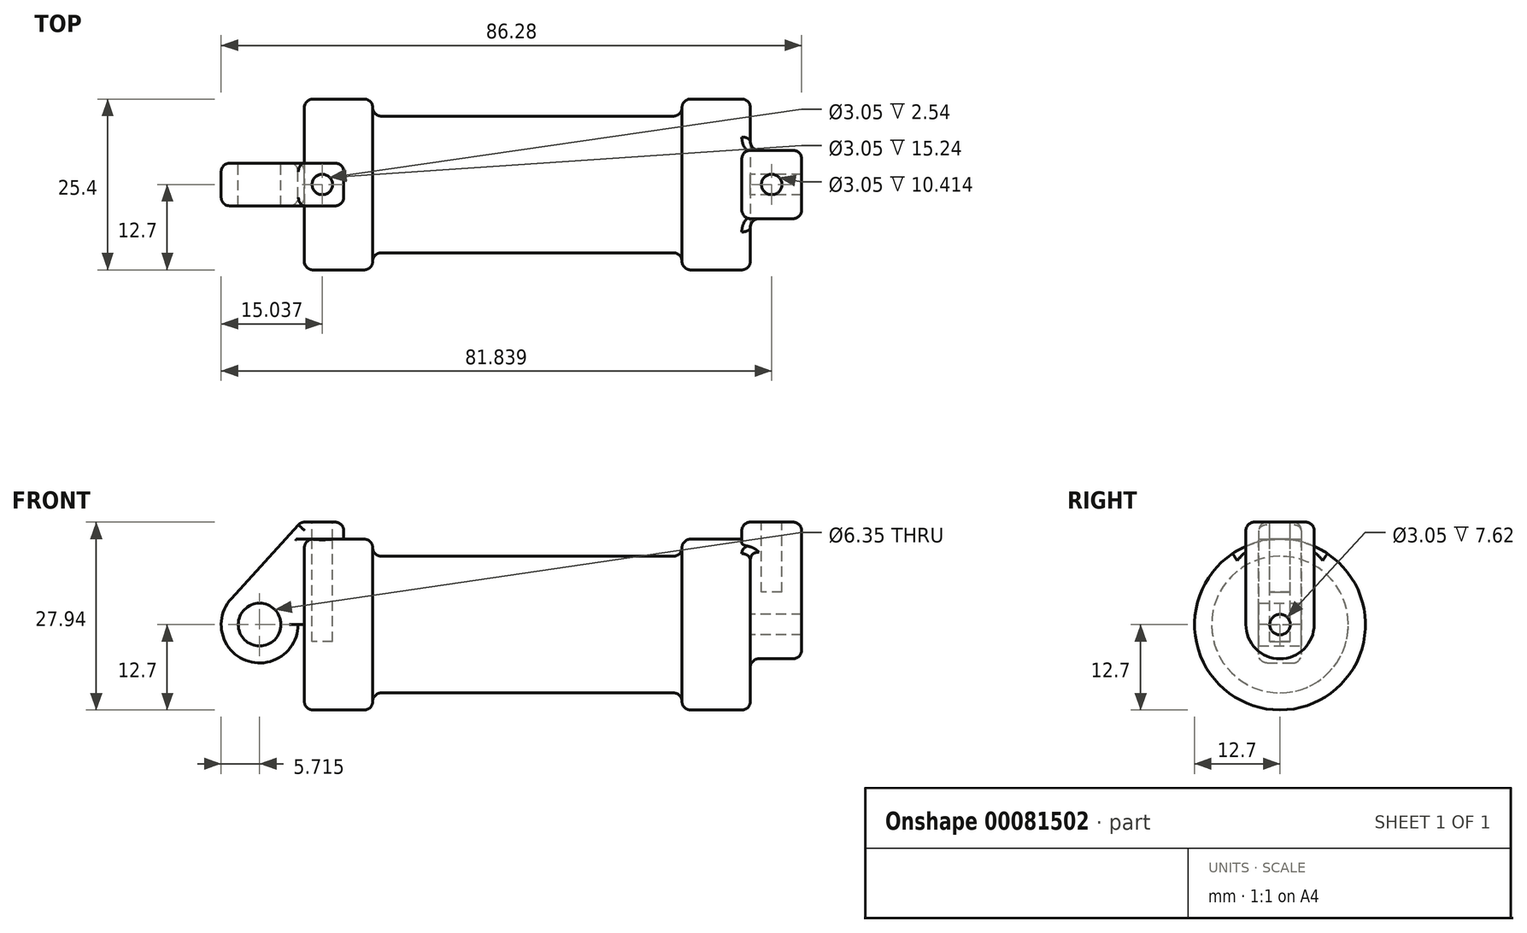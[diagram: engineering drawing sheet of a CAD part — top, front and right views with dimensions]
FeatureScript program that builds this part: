
annotation { "Feature Type Name" : "Feature", "Feature Type Description" : "" }
export const myFeature = defineFeature(function(context is Context, id is Id, definition is map)
    precondition{}
    {
        {
            var Q0;
            Q0=qCreatedBy(makeId("Front.planeOp"),FACE);
            var sketch = newSketch(context, id + "F0", { "sketchPlane" : qUnion([Q0])});
            skLineSegment(sketch, "E0", {"start": v(0, 0) * mm, "end": v(0, 12.7) * mm});
            skLineSegment(sketch, "E1", {"start": v(0, 12.7) * mm, "end": v(10.16, 12.7) * mm});
            skLineSegment(sketch, "E2", {"start": v(10.16, 12.7) * mm, "end": v(10.16, 10.16) * mm});
            skLineSegment(sketch, "E3", {"start": v(10.16, 10.16) * mm, "end": v(56.13, 10.16) * mm});
            skLineSegment(sketch, "E4", {"start": v(56.13, 10.16) * mm, "end": v(56.13, 12.7) * mm});
            skLineSegment(sketch, "E5", {"start": v(56.13, 12.7) * mm, "end": v(66.3, 12.7) * mm});
            skLineSegment(sketch, "E6", {"start": v(66.3, 12.7) * mm, "end": v(66.3, 0) * mm});
            skLineSegment(sketch, "E7", {"start": v(66.3, 0) * mm, "end": v(0, 0) * mm});
            skLineSegment(sketch, "E8", {"start": v(5.84, 15.24) * mm, "end": v(-0.5, 15.24) * mm});
            skLineSegment(sketch, "E9", {"start": v(-0.5, 15.24) * mm, "end": v(-10.88, 3.85) * mm});
            skLineSegment(sketch, "E10", {"start": v(0, 0) * mm, "end": v(-6.65, 0) * mm});
            skCircle(sketch, "E11", {"center": v(-6.65, 0) * mm, "radius": 5.72 * mm});
            skCircle(sketch, "E12", {"center": v(-6.65, 0) * mm, "radius": 3.18 * mm});
            skLineSegment(sketch, "E13", {"start": v(5.84, 15.24) * mm, "end": v(5.84, -9.4) * mm});
            skLineSegment(sketch, "E14", {"start": v(5.84, -9.4) * mm, "end": v(-8.18, -5.5) * mm});
            skSolve(sketch);
        }
        {
            var Q0;
            {var subQ0=sQuery(id+"F0.wireOp",EDGE,"E2");Q0=makeQuery(id+"F0.imprint","IMPRINT",FACE,{"disambiguationData":[TD([[makeQuery(id+"F0.imprint","IMPRINT",EDGE,{"derivedFrom":subQ0}),-1.0]])]});}
            var Q1;
            {var subQ0=sQuery(id+"F0.wireOp",EDGE,"E0");Q1=makeQuery(id+"F0.imprint","IMPRINT",FACE,{"disambiguationData":[TD([[makeQuery(id+"F0.imprint","IMPRINT",EDGE,{"derivedFrom":subQ0}),-1.0]])]});}
            var Q2;
            Q2=sQuery(id+"F0.wireOp",EDGE,"E7");
            revolve(context, id + "F1", {"entities" : qUnion([Q0, Q1]), "axis" : qUnion([Q2]), "revolveType" : RevolveType.FULL});
        }
        {
            var Q0;
            Q0=makeQuery(id+"F1.opRevolve","SWEPT_FACE",FACE,{"disambiguationData":[OSD([sQuery(id+"F0.wireOp",EDGE,"E6")])]});
            var sketch = newSketch(context, id + "F2", { "sketchPlane" : qUnion([Q0])});
            skCircle(sketch, "E15", {"center": v(0, 0) * mm, "radius": 1.52 * mm});
            skCircle(sketch, "E16", {"center": v(0, 0) * mm, "radius": 5.08 * mm});
            skLineSegment(sketch, "E17", {"start": v(-5.08, 0) * mm, "end": v(-5.08, 15.24) * mm});
            skLineSegment(sketch, "E18", {"start": v(5.08, 0) * mm, "end": v(5.08, 15.24) * mm});
            skLineSegment(sketch, "E19", {"start": v(-5.08, 15.24) * mm, "end": v(5.08, 15.24) * mm});
            skSolve(sketch);
        }
        {
            var Q0;
            {var subQ0=sQuery(id+"F2.wireOp",EDGE,"E17");var subQ1=sQuery(id+"F2.wireOp",EDGE,"E16");var subQ2=makeQuery(id+"F2.imprint","INTERSECT",VERTEX,{"derivedFrom":[subQ1,subQ0]});Q0=makeQuery(id+"F2.imprint","IMPRINT",FACE,{"disambiguationData":[TD([[makeQuery(id+"F2.imprint","IMPRINT",EDGE,{"disambiguationData":[TD([[subQ2,1.0]])],"derivedFrom":subQ1}),-1.0]])]});}
            var Q1;
            Q1=makeQuery(id+"F2.imprint","IMPRINT",FACE,{"disambiguationData":[TD([[makeQuery(id+"F2.imprint","IMPRINT",EDGE,{"derivedFrom":sQuery(id+"F2.wireOp",EDGE,"E15")}),-1.0]])]});
            var Q2;
            {var subQ0=sQuery(id+"F2.wireOp",EDGE,"E19");Q2=makeQuery(id+"F2.imprint","IMPRINT",FACE,{"disambiguationData":[TD([[makeQuery(id+"F2.imprint","IMPRINT",EDGE,{"derivedFrom":subQ0}),-1.0]])]});}
            extrude(context, id + "F3", {"entities" : qUnion([Q0, Q1, Q2]), "operationType" : NewBodyOperationType.ADD, "depth" : 7.62 * mm});
        }
        {
            var Q0;
            Q0=makeQuery(id+"F3.opExtrude","CAP_FACE",FACE,{"disambiguationData":[OSD([sQuery(id+"F2.wireOp",EDGE,"E15"),sQuery(id+"F2.wireOp",EDGE,"E16"),sQuery(id+"F2.wireOp",EDGE,"E17"),sQuery(id+"F2.wireOp",EDGE,"E18"),sQuery(id+"F2.wireOp",EDGE,"E19")])],"isStart":true});
            extrude(context, id + "F4", {"entities" : qUnion([Q0]), "operationType" : NewBodyOperationType.ADD, "depth" : 1.27 * mm});
        }
        {
            var Q0;
            {var subQ3=sQuery(id+"F0.wireOp",EDGE,"E0");Q0=makeQuery(id+"F0.imprint","IMPRINT",FACE,{"disambiguationData":[TD([[makeQuery(id+"F0.imprint","IMPRINT",EDGE,{"derivedFrom":subQ3}),1.0]])]});}
            var Q1;
            {var subQ4=sQuery(id+"F0.wireOp",EDGE,"E12");Q1=makeQuery(id+"F0.imprint","IMPRINT",FACE,{"disambiguationData":[TD([[makeQuery(id+"F0.imprint","IMPRINT",EDGE,{"derivedFrom":subQ4}),-1.0]])]});}
            extrude(context, id + "F5", {"entities" : qUnion([Q0, Q1]), "endBound" : BoundingType.SYMMETRIC, "depth" : 6.35 * mm});
        }
        {
            var Q0;
            Q0=makeQuery(id+"F5.opExtrude","SWEPT_FACE",FACE,{"disambiguationData":[OSD([sQuery(id+"F0.wireOp",EDGE,"E8")])]});
            var sketch = newSketch(context, id + "F6", { "sketchPlane" : qUnion([Q0])});
            skCircle(sketch, "E20", {"center": v(2.67, 0) * mm, "radius": 1.52 * mm});
            skSolve(sketch);
        }
        {
            var Q0;
            {var subQ0=sQuery(id+"F2.wireOp",EDGE,"E19");Q0=makeQuery(id+"F4.boolean.opBoolean","MERGE",FACE,{"derivedFrom":[makeQuery(id+"F3.opExtrude","SWEPT_FACE",FACE,{"disambiguationData":[OSD([subQ0])]}),makeQuery(id+"F4.opExtrude","SWEPT_FACE",FACE,{"disambiguationData":[OSD([subQ0])]})]});}
            var sketch = newSketch(context, id + "F7", { "sketchPlane" : qUnion([Q0])});
            skCircle(sketch, "E21", {"center": v(69.47, 0) * mm, "radius": 1.52 * mm});
            skSolve(sketch);
        }
        {
            var Q0;
            Q0=makeQuery(id+"F6.imprint","IMPRINT",FACE,{"disambiguationData":[TD([[makeQuery(id+"F6.imprint","IMPRINT",EDGE,{"derivedFrom":sQuery(id+"F6.wireOp",EDGE,"E20")}),1.0]])]});
            extrude(context, id + "F8", {"entities" : qUnion([Q0]), "operationType" : NewBodyOperationType.REMOVE, "oppositeDirection" : true, "depth" : 17.78 * mm});
        }
        {
            var Q0;
            Q0=makeQuery(id+"F7.imprint","IMPRINT",FACE,{"disambiguationData":[TD([[makeQuery(id+"F7.imprint","IMPRINT",EDGE,{"derivedFrom":sQuery(id+"F7.wireOp",EDGE,"E21")}),1.0]])]});
            extrude(context, id + "F9", {"entities" : qUnion([Q0]), "operationType" : NewBodyOperationType.REMOVE, "oppositeDirection" : true, "depth" : 10.4 * mm});
        }
        {
            var Q0;
            Q0=makeQuery(id+"F5.opExtrude","CAP_EDGE",EDGE,{"disambiguationData":[OSD([sQuery(id+"F0.wireOp",EDGE,"E8")])],"isStart":false});
            var Q1;
            Q1=makeQuery(id+"F5.opExtrude","CAP_EDGE",EDGE,{"disambiguationData":[OSD([sQuery(id+"F0.wireOp",EDGE,"E9")])],"isStart":false});
            var Q2;
            Q2=makeQuery(id+"F1.opRevolve","SWEPT_EDGE",EDGE,{"disambiguationData":[OSD([sQuery(id+"F0.wireOp",EDGE,"E0"),sQuery(id+"F0.wireOp",EDGE,"E1")])]});
            var Q3;
            Q3=makeQuery(id+"F5.opExtrude","CAP_EDGE",EDGE,{"disambiguationData":[OSD([sQuery(id+"F0.wireOp",EDGE,"E11")])],"isStart":false});
            var Q4;
            Q4=makeQuery(id+"F5.opExtrude","CAP_EDGE",EDGE,{"disambiguationData":[OSD([sQuery(id+"F0.wireOp",EDGE,"E13")])],"isStart":false});
            fillet(context, id + "F10", {"entities" : qUnion([Q0, Q1, Q2, Q3, Q4]), "radius" : 1.27 * mm, "tangentPropagation" : true, "allowEdgeOverflow" : false});
        }
        {
            var Q0;
            Q0=makeQuery(id+"F5.opExtrude","CAP_EDGE",EDGE,{"disambiguationData":[OSD([sQuery(id+"F0.wireOp",EDGE,"E0")])],"isStart":true});
            var Q1;
            Q1=makeQuery(id+"F5.opExtrude","CAP_EDGE",EDGE,{"disambiguationData":[OSD([sQuery(id+"F0.wireOp",EDGE,"E0")])],"isStart":false});
            var Q2;
            Q2=makeQuery(id+"F4.opExtrude","CAP_EDGE",EDGE,{"disambiguationData":[OSD([sQuery(id+"F2.wireOp",EDGE,"E18")])],"isStart":false});
            var Q3;
            Q3=makeQuery(id+"F4.opExtrude","CAP_EDGE",EDGE,{"disambiguationData":[OSD([sQuery(id+"F2.wireOp",EDGE,"E17")])],"isStart":false});
            var Q4;
            Q4=makeQuery(id+"F5.opExtrude","SWEPT_EDGE",EDGE,{"disambiguationData":[OSD([sQuery(id+"F0.wireOp",EDGE,"E8"),sQuery(id+"F0.wireOp",EDGE,"E9")])]});
            var Q5;
            Q5=makeQuery(id+"F4.opExtrude","CAP_EDGE",EDGE,{"disambiguationData":[OSD([sQuery(id+"F2.wireOp",EDGE,"E19")])],"isStart":false});
            var Q6;
            Q6=makeQuery(id+"F5.opExtrude","CAP_EDGE",EDGE,{"disambiguationData":[OSD([sQuery(id+"F0.wireOp",EDGE,"E13")])],"isStart":true});
            var Q7;
            Q7=makeQuery(id+"F5.opExtrude","CAP_EDGE",EDGE,{"disambiguationData":[OSD([sQuery(id+"F0.wireOp",EDGE,"E8")])],"isStart":true});
            fillet(context, id + "F11", {"entities" : qUnion([Q0, Q1, Q2, Q3, Q4, Q5, Q6, Q7]), "radius" : 1.27 * mm, "tangentPropagation" : true, "allowEdgeOverflow" : false});
        }
        {
            var Q0;
            Q0=makeQuery(id+"F5.opExtrude","CAP_EDGE",EDGE,{"disambiguationData":[OSD([sQuery(id+"F0.wireOp",EDGE,"E11")])],"isStart":true});
            var Q1;
            {var subQ0=sQuery(id+"F0.wireOp",EDGE,"E0");Q1=makeQuery(id+"F11.opFillet","BLEND_EDGE",EDGE,{"blendedFrom":[makeQuery(id+"F5.opExtrude","CAP_EDGE",EDGE,{"disambiguationData":[OSD([subQ0])],"isStart":true}),makeQuery(id+"F5.opExtrude","CAP_FACE",FACE,{"disambiguationData":[OSD([subQ0,sQuery(id+"F0.wireOp",EDGE,"E1"),sQuery(id+"F0.wireOp",EDGE,"E8"),sQuery(id+"F0.wireOp",EDGE,"E9"),sQuery(id+"F0.wireOp",EDGE,"E10"),sQuery(id+"F0.wireOp",EDGE,"E11"),sQuery(id+"F0.wireOp",EDGE,"E12"),sQuery(id+"F0.wireOp",EDGE,"E13")])],"isStart":true})],"blendedInto":[makeQuery(id+"F5.opExtrude","CAP_FACE",FACE,{"disambiguationData":[OSD([subQ0,sQuery(id+"F0.wireOp",EDGE,"E1"),sQuery(id+"F0.wireOp",EDGE,"E8"),sQuery(id+"F0.wireOp",EDGE,"E9"),sQuery(id+"F0.wireOp",EDGE,"E10"),sQuery(id+"F0.wireOp",EDGE,"E11"),sQuery(id+"F0.wireOp",EDGE,"E12"),sQuery(id+"F0.wireOp",EDGE,"E13")])],"isStart":true})]});}
            fillet(context, id + "F12", {"entities" : qUnion([Q0, Q1]), "radius" : 1.27 * mm, "tangentPropagation" : true, "allowEdgeOverflow" : false});
        }
        {
            var Q0;
            Q0=makeQuery(id+"F3.opExtrude","CAP_EDGE",EDGE,{"disambiguationData":[OSD([sQuery(id+"F2.wireOp",EDGE,"E16")])],"isStart":false});
            var Q1;
            Q1=makeQuery(id+"F3.opExtrude","CAP_EDGE",EDGE,{"disambiguationData":[OSD([sQuery(id+"F2.wireOp",EDGE,"E18")])],"isStart":false});
            var Q2;
            Q2=makeQuery(id+"F3.opExtrude","CAP_EDGE",EDGE,{"disambiguationData":[OSD([sQuery(id+"F2.wireOp",EDGE,"E17")])],"isStart":false});
            fillet(context, id + "F13", {"entities" : qUnion([Q0, Q1, Q2]), "radius" : 1.27 * mm, "tangentPropagation" : true, "allowEdgeOverflow" : false});
        }
        {
            var Q0;
            {var subQ0=sQuery(id+"F2.wireOp",EDGE,"E16");var subQ1=sQuery(id+"F2.wireOp",EDGE,"E18");Q0=makeQuery(id+"F3.boolean.opBoolean","SPLIT",EDGE,{"disambiguationData":[TD([makeQuery(id+"F3.opExtrude","SWEPT_FACE",FACE,{"disambiguationData":[OSD([subQ0])]})])],"derivedFrom":makeQuery(id+"F3.opExtrude","CAP_EDGE",EDGE,{"disambiguationData":[OSD([subQ1])],"isStart":true})});}
            var Q1;
            Q1=makeQuery(id+"F3.opExtrude","CAP_EDGE",EDGE,{"disambiguationData":[OSD([sQuery(id+"F2.wireOp",EDGE,"E16")])],"isStart":true});
            var Q2;
            {var subQ0=sQuery(id+"F2.wireOp",EDGE,"E17");Q2=makeQuery(id+"F13.opFillet","BLEND_EDGE",EDGE,{"blendedFrom":[makeQuery(id+"F3.opExtrude","CAP_EDGE",EDGE,{"disambiguationData":[OSD([subQ0])],"isStart":false}),makeQuery(id+"F4.boolean.opBoolean","MERGE",FACE,{"derivedFrom":[makeQuery(id+"F3.opExtrude","SWEPT_FACE",FACE,{"disambiguationData":[OSD([subQ0])]}),makeQuery(id+"F4.opExtrude","SWEPT_FACE",FACE,{"disambiguationData":[OSD([subQ0])]})]})],"blendedInto":[makeQuery(id+"F4.boolean.opBoolean","MERGE",FACE,{"derivedFrom":[makeQuery(id+"F3.opExtrude","SWEPT_FACE",FACE,{"disambiguationData":[OSD([subQ0])]}),makeQuery(id+"F4.opExtrude","SWEPT_FACE",FACE,{"disambiguationData":[OSD([subQ0])]})]})]});}
            var Q3;
            {var subQ0=sQuery(id+"F2.wireOp",EDGE,"E16");var subQ1=sQuery(id+"F2.wireOp",EDGE,"E17");Q3=makeQuery(id+"F3.boolean.opBoolean","SPLIT",EDGE,{"disambiguationData":[TD([makeQuery(id+"F3.opExtrude","SWEPT_FACE",FACE,{"disambiguationData":[OSD([subQ0])]})])],"derivedFrom":makeQuery(id+"F3.opExtrude","CAP_EDGE",EDGE,{"disambiguationData":[OSD([subQ1])],"isStart":true})});}
            var Q4;
            {var subQ0=sQuery(id+"F2.wireOp",EDGE,"E18");Q4=makeQuery(id+"F13.opFillet","BLEND_EDGE",EDGE,{"blendedFrom":[makeQuery(id+"F3.opExtrude","CAP_EDGE",EDGE,{"disambiguationData":[OSD([subQ0])],"isStart":false}),makeQuery(id+"F4.boolean.opBoolean","MERGE",FACE,{"derivedFrom":[makeQuery(id+"F3.opExtrude","SWEPT_FACE",FACE,{"disambiguationData":[OSD([subQ0])]}),makeQuery(id+"F4.opExtrude","SWEPT_FACE",FACE,{"disambiguationData":[OSD([subQ0])]})]})],"blendedInto":[makeQuery(id+"F4.boolean.opBoolean","MERGE",FACE,{"derivedFrom":[makeQuery(id+"F3.opExtrude","SWEPT_FACE",FACE,{"disambiguationData":[OSD([subQ0])]}),makeQuery(id+"F4.opExtrude","SWEPT_FACE",FACE,{"disambiguationData":[OSD([subQ0])]})]})]});}
            fillet(context, id + "F14", {"entities" : qUnion([Q0, Q1, Q2, Q3, Q4]), "radius" : 1.27 * mm, "tangentPropagation" : true, "allowEdgeOverflow" : false});
        }
        {
            var Q0;
            {var subQ0=makeQuery(id+"F1.opRevolve","SWEPT_FACE",FACE,{"disambiguationData":[OSD([sQuery(id+"F0.wireOp",EDGE,"E5")])]});var subQ1=sQuery(id+"F2.wireOp",EDGE,"E16");var subQ2=sQuery(id+"F2.wireOp",EDGE,"E17");Q0=makeQuery(id+"F14.opFillet","BLEND_EDGE",EDGE,{"blendedFrom":[makeQuery(id+"F3.boolean.opBoolean","SPLIT",EDGE,{"disambiguationData":[TD([makeQuery(id+"F3.opExtrude","SWEPT_FACE",FACE,{"disambiguationData":[OSD([subQ1])]})])],"derivedFrom":makeQuery(id+"F3.opExtrude","CAP_EDGE",EDGE,{"disambiguationData":[OSD([subQ2])],"isStart":true})}),subQ0],"blendedInto":[subQ0]});}
            var Q1;
            {var subQ0=makeQuery(id+"F1.opRevolve","SWEPT_FACE",FACE,{"disambiguationData":[OSD([sQuery(id+"F0.wireOp",EDGE,"E5")])]});var subQ1=sQuery(id+"F2.wireOp",EDGE,"E16");var subQ2=sQuery(id+"F2.wireOp",EDGE,"E18");Q1=makeQuery(id+"F14.opFillet","BLEND_EDGE",EDGE,{"blendedFrom":[makeQuery(id+"F3.boolean.opBoolean","SPLIT",EDGE,{"disambiguationData":[TD([makeQuery(id+"F3.opExtrude","SWEPT_FACE",FACE,{"disambiguationData":[OSD([subQ1])]})])],"derivedFrom":makeQuery(id+"F3.opExtrude","CAP_EDGE",EDGE,{"disambiguationData":[OSD([subQ2])],"isStart":true})}),subQ0],"blendedInto":[subQ0]});}
            var Q2;
            Q2=makeQuery(id+"F3.opExtrude","CAP_EDGE",EDGE,{"disambiguationData":[OSD([sQuery(id+"F2.wireOp",EDGE,"E19")])],"isStart":false});
            fillet(context, id + "F15", {"entities" : qUnion([Q0, Q1, Q2]), "radius" : 1.27 * mm, "tangentPropagation" : true, "allowEdgeOverflow" : false});
        }
        {
            var Q0;
            Q0=makeQuery(id+"F1.opRevolve","SWEPT_EDGE",EDGE,{"disambiguationData":[OSD([sQuery(id+"F0.wireOp",EDGE,"E3"),sQuery(id+"F0.wireOp",EDGE,"E4")])]});
            var Q1;
            Q1=makeQuery(id+"F1.opRevolve","SWEPT_EDGE",EDGE,{"disambiguationData":[OSD([sQuery(id+"F0.wireOp",EDGE,"E2"),sQuery(id+"F0.wireOp",EDGE,"E3")])]});
            fillet(context, id + "F16", {"entities" : qUnion([Q0, Q1]), "radius" : 1.27 * mm, "tangentPropagation" : true, "allowEdgeOverflow" : false});
        }
        {
            var Q0;
            Q0=makeQuery(id+"F1.opRevolve","SWEPT_EDGE",EDGE,{"disambiguationData":[OSD([sQuery(id+"F0.wireOp",EDGE,"E1"),sQuery(id+"F0.wireOp",EDGE,"E2")])]});
            var Q1;
            Q1=makeQuery(id+"F1.opRevolve","SWEPT_EDGE",EDGE,{"disambiguationData":[OSD([sQuery(id+"F0.wireOp",EDGE,"E4"),sQuery(id+"F0.wireOp",EDGE,"E5")])]});
            fillet(context, id + "F17", {"entities" : qUnion([Q0, Q1]), "radius" : 1.27 * mm, "tangentPropagation" : true, "allowEdgeOverflow" : false});
        }
        {
            var Q0;
            Q0=makeQuery(id+"F5.opExtrude","SWEPT_EDGE",EDGE,{"disambiguationData":[OSD([sQuery(id+"F0.wireOp",EDGE,"E8"),sQuery(id+"F0.wireOp",EDGE,"E13")])]});
            fillet(context, id + "F18", {"entities" : qUnion([Q0]), "radius" : 1.27 * mm, "tangentPropagation" : true, "allowEdgeOverflow" : false});
        }
    });
